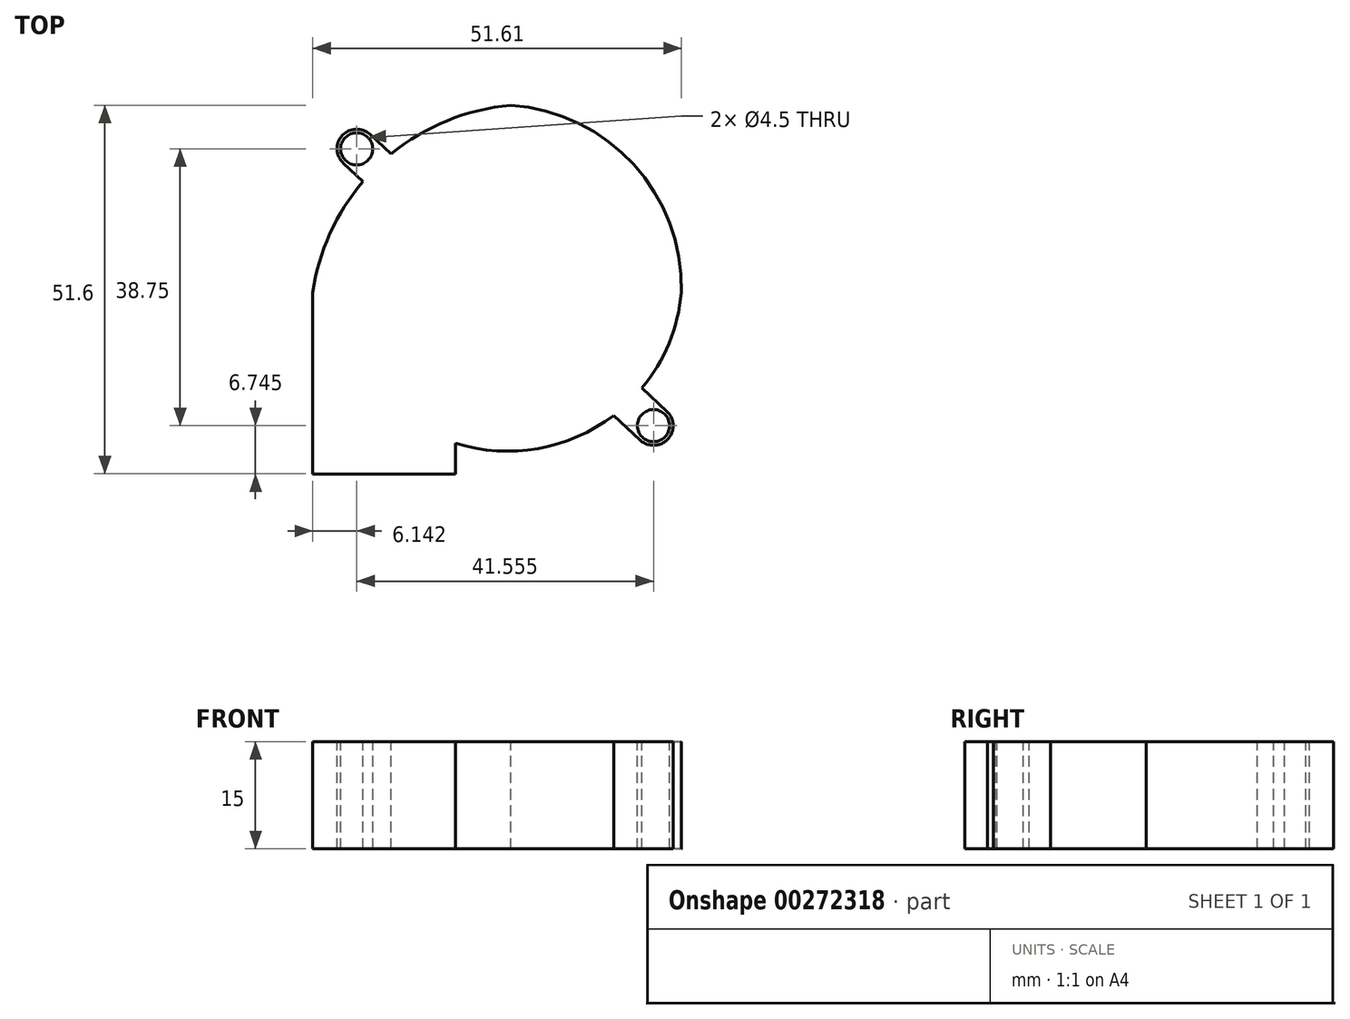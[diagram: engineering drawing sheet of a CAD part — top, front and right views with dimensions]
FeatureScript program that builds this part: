
annotation { "Feature Type Name" : "Feature", "Feature Type Description" : "" }
export const myFeature = defineFeature(function(context is Context, id is Id, definition is map)
    precondition{}
    {
        {
            var Q0;
            Q0=qCreatedBy(makeId("Top.planeOp"),FACE);
            var sketch = newSketch(context, id + "F0", { "sketchPlane" : qUnion([Q0])});
            skLineSegment(sketch, "E0", {"start": v(-37.77, 0) * mm, "end": v(36.58, 0) * mm, "construction": true});
            skLineSegment(sketch, "E1", {"start": v(0, 27.57) * mm, "end": v(0, -32.06) * mm, "construction": true});
            skCircle(sketch, "E2", {"center": v(-23, 21.1) * mm, "radius": 2.25 * mm});
            skCircle(sketch, "E3", {"center": v(20, -18.35) * mm, "radius": 2.25 * mm});
            skLineSegment(sketch, "E4", {"start": v(-23, 21.1) * mm, "end": v(20, -18.35) * mm, "construction": true});
            skPoint(sketch, "E5", {"position": v(0, 0) * mm});
            skCircle(sketch, "E6", {"center": v(-23, 21.1) * mm, "radius": 2.75 * mm});
            skCircle(sketch, "E7", {"center": v(20, -18.35) * mm, "radius": 2.75 * mm});
            skLineSegment(sketch, "E8", {"start": v(-28.95, 0) * mm, "end": v(-28.95, -27.52) * mm});
            skLineSegment(sketch, "E9", {"start": v(-28.95, -27.52) * mm, "end": v(-8.95, -27.52) * mm});
            skLineSegment(sketch, "E10", {"start": v(-8.95, -27.52) * mm, "end": v(-8.95, -24.52) * mm});
            skArc(sketch, "E11", {"start": v(-8.95, -24.52) * mm, "mid": v(16.46, 16.63) * mm, "end": v(-28.95, 0) * mm});
            skLineSegment(sketch, "E12", {"start": v(-24.86, 19.07) * mm, "end": v(-21.14, 23.13) * mm, "construction": true});
            skLineSegment(sketch, "E13", {"start": v(-24.86, 19.07) * mm, "end": v(-22.92, 16.96) * mm});
            skLineSegment(sketch, "E14", {"start": v(-21.14, 23.13) * mm, "end": v(-18.5, 21.1) * mm});
            skLineSegment(sketch, "E15", {"start": v(21.86, -16.32) * mm, "end": v(18.14, -20.37) * mm, "construction": true});
            skLineSegment(sketch, "E16", {"start": v(21.86, -16.32) * mm, "end": v(18.57, -12.73) * mm});
            skLineSegment(sketch, "E17", {"start": v(18.14, -20.37) * mm, "end": v(14.67, -17.7) * mm});
            skLineSegment(sketch, "E18", {"start": v(-28.95, 0) * mm, "end": v(-28.95, 37.17) * mm, "construction": true});
            skLineSegment(sketch, "E19.bottom", {"start": v(27.1, -174.61) * mm, "end": v(78.7, -174.61) * mm, "construction": true});
            skLineSegment(sketch, "E19.top", {"start": v(27.1, -226.21) * mm, "end": v(78.7, -226.21) * mm, "construction": true});
            skLineSegment(sketch, "E19.left", {"start": v(27.1, -174.61) * mm, "end": v(27.1, -226.21) * mm, "construction": true});
            skLineSegment(sketch, "E19.right", {"start": v(78.7, -174.61) * mm, "end": v(78.7, -226.21) * mm, "construction": true});
            skLineSegment(sketch, "E20", {"start": v(27.1, -226.21) * mm, "end": v(47.1, -226.21) * mm});
            skLineSegment(sketch, "E21", {"start": v(47.1, -226.21) * mm, "end": v(47.1, -221.91) * mm});
            skLineSegment(sketch, "E22", {"start": v(54.8, -174.61) * mm, "end": v(54.8, -226.21) * mm, "construction": true});
            skLineSegment(sketch, "E23", {"start": v(27.1, -200.81) * mm, "end": v(78.7, -200.81) * mm, "construction": true});
            skCircle(sketch, "E24", {"center": v(33.24, -180.71) * mm, "radius": 2.25 * mm});
            skCircle(sketch, "E25", {"center": v(74.8, -219.46) * mm, "radius": 2.25 * mm});
            skCircle(sketch, "E26", {"center": v(74.8, -219.46) * mm, "radius": 2.75 * mm});
            skLineSegment(sketch, "E27", {"start": v(33.24, -180.71) * mm, "end": v(74.8, -219.46) * mm, "construction": true});
            skPoint(sketch, "E28", {"position": v(54.8, -200.81) * mm});
            skLineSegment(sketch, "E29", {"start": v(27.1, -226.21) * mm, "end": v(27.1, -200.81) * mm});
            skArc(sketch, "E30", {"start": v(47.1, -221.91) * mm, "mid": v(67.95, -218.93) * mm, "end": v(78.7, -200.81) * mm});
            skArc(sketch, "E31", {"start": v(54.8, -174.61) * mm, "mid": v(36.39, -182.9) * mm, "end": v(27.1, -200.81) * mm});
            skArc(sketch, "E32", {"start": v(78.7, -200.81) * mm, "mid": v(72.02, -182.9) * mm, "end": v(54.8, -174.61) * mm});
            skCircle(sketch, "E33", {"center": v(33.24, -180.71) * mm, "radius": 2.75 * mm});
            skLineSegment(sketch, "E34", {"start": v(31.37, -182.73) * mm, "end": v(35.12, -178.7) * mm, "construction": true});
            skLineSegment(sketch, "E35", {"start": v(31.37, -182.73) * mm, "end": v(34.11, -185.29) * mm});
            skLineSegment(sketch, "E36", {"start": v(35.12, -178.7) * mm, "end": v(38.04, -181.43) * mm});
            skLineSegment(sketch, "E37", {"start": v(72.92, -221.48) * mm, "end": v(76.67, -217.45) * mm, "construction": true});
            skLineSegment(sketch, "E38", {"start": v(76.67, -217.45) * mm, "end": v(73.19, -214.2) * mm});
            skLineSegment(sketch, "E39", {"start": v(72.92, -221.48) * mm, "end": v(69.22, -218.02) * mm});
            skSolve(sketch);
        }
        {
            var Q0;
            {var subQ0=sQuery(id+"F0.wireOp",EDGE,"E35");Q0=makeQuery(id+"F0.imprint","IMPRINT",FACE,{"disambiguationData":[TD([[makeQuery(id+"F0.imprint","IMPRINT",EDGE,{"derivedFrom":subQ0}),1.0]])]});}
            var Q1;
            Q1=makeQuery(id+"F0.imprint","IMPRINT",FACE,{"disambiguationData":[TD([[makeQuery(id+"F0.imprint","IMPRINT",EDGE,{"derivedFrom":sQuery(id+"F0.wireOp",EDGE,"E20")}),1.0]])]});
            var Q2;
            Q2=makeQuery(id+"F0.imprint","IMPRINT",FACE,{"disambiguationData":[TD([[makeQuery(id+"F0.imprint","IMPRINT",EDGE,{"derivedFrom":sQuery(id+"F0.wireOp",EDGE,"E24")}),-1.0]])]});
            var Q3;
            {var subQ0=sQuery(id+"F0.wireOp",EDGE,"E38");Q3=makeQuery(id+"F0.imprint","IMPRINT",FACE,{"disambiguationData":[TD([[makeQuery(id+"F0.imprint","IMPRINT",EDGE,{"derivedFrom":subQ0}),1.0]])]});}
            var Q4;
            Q4=makeQuery(id+"F0.imprint","IMPRINT",FACE,{"disambiguationData":[TD([[makeQuery(id+"F0.imprint","IMPRINT",EDGE,{"derivedFrom":sQuery(id+"F0.wireOp",EDGE,"E25")}),-1.0]])]});
            extrude(context, id + "F1", {"entities" : qUnion([Q0, Q1, Q2, Q3, Q4]), "oppositeDirection" : true, "depth" : 15 * mm});
        }
    });
